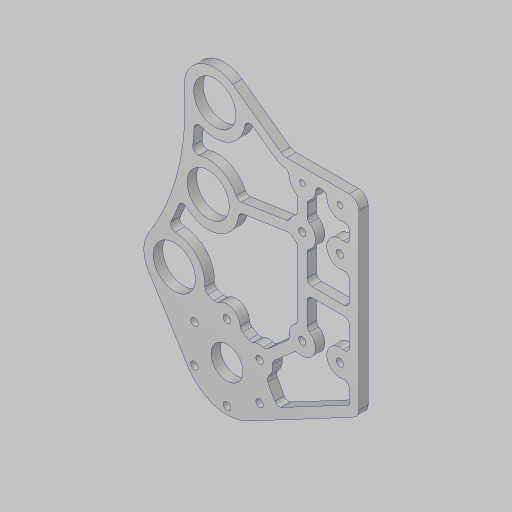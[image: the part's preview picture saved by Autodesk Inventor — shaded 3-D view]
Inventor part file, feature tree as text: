
AUTODESK INVENTOR PART (.ipt)
format: ipt  version: 2023.5 (Build 275446000, 446)  size: 446,976 bytes
history: native  units: in
note: dims shown in document units (in); Inventor stores cm internally (conversion verified against a paired STEP export)
features: sketch x4, hole x3, extrude x2, fillet x2, projected_geometry x2
ambient origin geometry x8: Origin, YZ Plane, XZ Plane, XY Plane, X Axis, Y Axis, Z Axis, Center Point
bodies: Solid1 (feature_tree)
feature tree (13):
  sketch  "Sketch1"  dims[d0=2.0in d1=15.0in]
  sketch  "Sketch2"  dims[d2=0.875in d3=17.0in d4=2.0in]
  extrude  "Extrusion1"  Depth=2.0in
  hole  "Hole1"  [1 undecoded]
  fillet  "Fillet1"  Radius=2.0in
  hole  "Hole2"  [1 undecoded]
  hole  "Hole3"  [1 undecoded]
  extrude  "Extrusion2"  Depth=0.25in
  fillet  "Fillet2"  Radius=3.6in
  sketch  "Sketch3"  dims[d5=17.0in d6=1.0in]
  projected_geometry  "Projected Loop1"
  sketch  "Sketch4"  dims[d7=0.2405in d8=2.4in d9=0.5in d10=3.6in d11=1.5in d12=1.5in d13=0.9in d14=3.7in d15=1.0in d16=3.4in d17=3.0in d20=2.0in d22=1.125in d23=4.297in d24=0.25in d25=2.0in d26=2.3622in d28=360.0deg d30=7.0in d31=2.0in d32=0.201in d33=1.0in d34=1.5in d35=1.0in d36=0.201in d37=1.0in d38=1.0in d39=2.5in d40=0.25in d41=0.0in d42=0.85in d43=0.201in d44=0.75in d45=0.385in d46=0.25in d47=0.5635in d48=1.0in d49=0.8108in d50=0.375in d51=0.26in d52=1.825in d53=0.156in d54=0.38in d55=0.385in d56=0.25in d57=0.5635in d58=1.0in d59=0.8108in d60=0.25in d61=0.25in d62=0.25in d63=0.25in d64=0.25in d65=0.25in d66=0.125in d67=0.125in d68=0.125in d69=0.125in d70=2.5in d71=0.125in d72=0.125in d73=0.125in d74=0.125in d75=1.0in d76=0.0in d77=0.0in d78=0.13in d81=1.75in d82=0.875in d83=0.156in d84=0.38in d85=0.375in d86=0.25in d87=0.5635in d88=1.0in d89=0.8108in d90=0.125in d91=0.125in]
  projected_geometry  "Projected Loop2"
note: 3 required parameter values undecoded (feature->parameter linkage not recoverable at this tier; creation-order binding heuristic only, values carry confidence <= 0.55)
